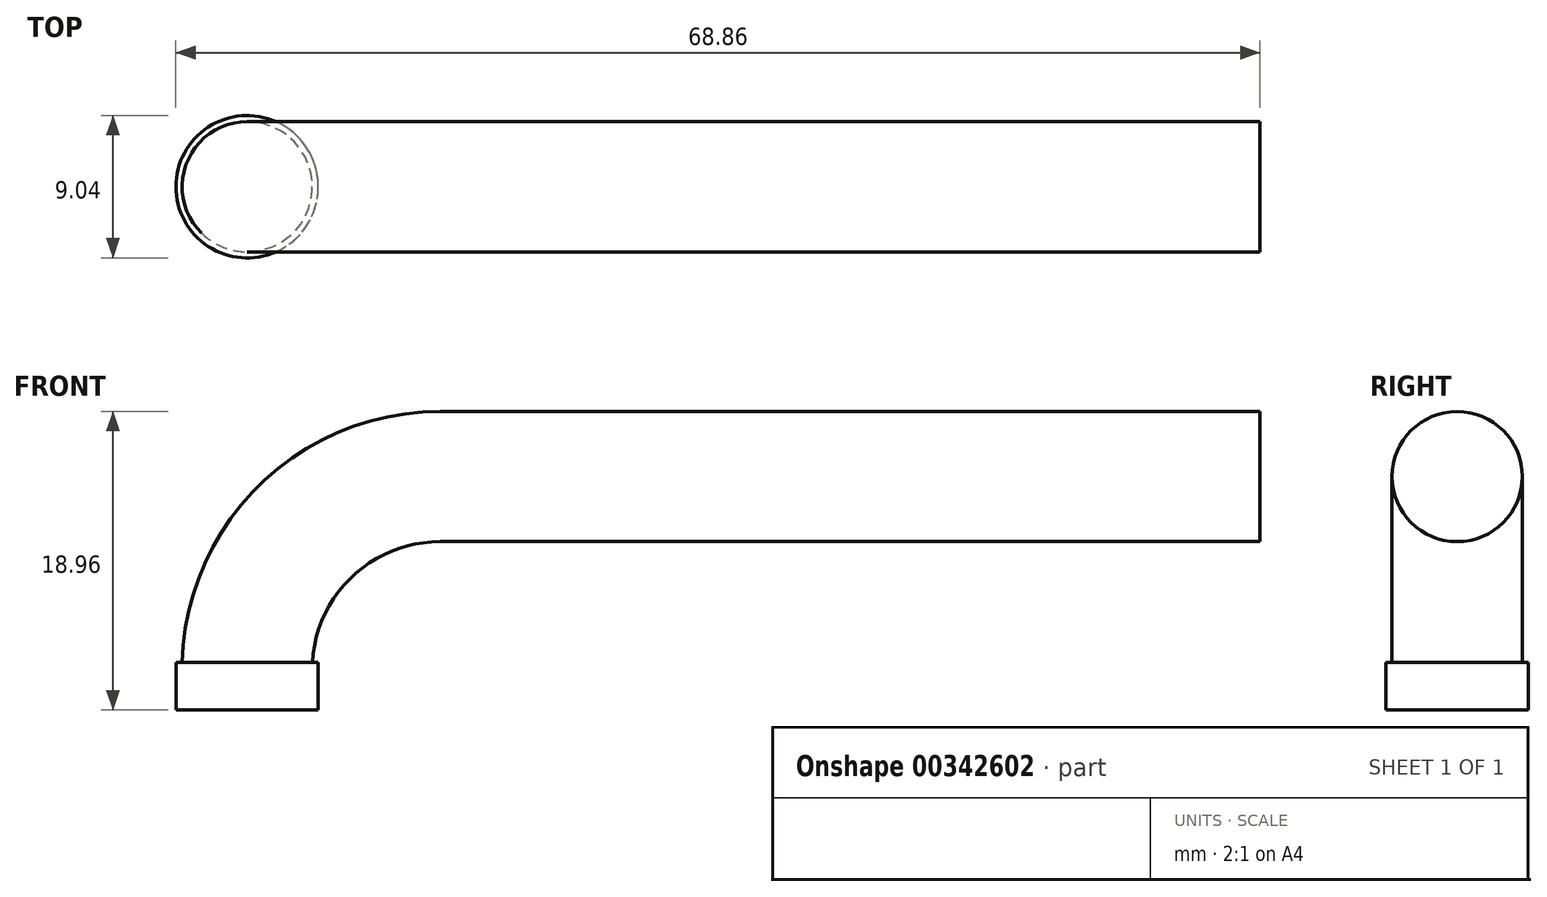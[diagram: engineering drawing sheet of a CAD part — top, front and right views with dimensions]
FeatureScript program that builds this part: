
annotation { "Feature Type Name" : "Feature", "Feature Type Description" : "" }
export const myFeature = defineFeature(function(context is Context, id is Id, definition is map)
    precondition{}
    {
        {
            var Q0;
            Q0=qCreatedBy(makeId("Front.planeOp"),FACE);
            var sketch = newSketch(context, id + "F0", { "sketchPlane" : qUnion([Q0])});
            skLineSegment(sketch, "E0", {"start": v(0, 28.7) * mm, "end": v(-52.1, 28.7) * mm});
            skArc(sketch, "E1", {"start": v(-52.1, 28.7) * mm, "mid": v(-60.75, 25.12) * mm, "end": v(-64.33, 16.46) * mm});
            skLineSegment(sketch, "E2", {"start": v(-52.1, 16.46) * mm, "end": v(-52.1, 28.7) * mm});
            skLineSegment(sketch, "E3", {"start": v(-52.1, 16.46) * mm, "end": v(-64.33, 16.46) * mm});
            skLineSegment(sketch, "E4", {"start": v(-64.33, 16.46) * mm, "end": v(-64.33, 13.88) * mm});
            skSolve(sketch);
        }
        {
            var Q0;
            Q0=qCreatedBy(makeId("Right.planeOp"),FACE);
            var sketch = newSketch(context, id + "F1", { "sketchPlane" : qUnion([Q0])});
            skCircle(sketch, "E5", {"center": v(0, 28.7) * mm, "radius": 4.14 * mm});
            skSolve(sketch);
        }
        {
            var Q0;
            Q0=makeQuery(id+"F1.imprint","IMPRINT",FACE,{"disambiguationData":[TD([[makeQuery(id+"F1.imprint","IMPRINT",EDGE,{"derivedFrom":sQuery(id+"F1.wireOp",EDGE,"E5")}),1.0]])]});
            var Q1;
            Q1=sQuery(id+"F0.wireOp",EDGE,"E0");
            var Q2;
            Q2=sQuery(id+"F0.wireOp",EDGE,"E1");
            var Q3;
            Q3=sQuery(id+"F0.wireOp",EDGE,"E4");
            sweep(context, id + "F2", {"profiles" : qUnion([Q0]), "path" : qUnion([Q1, Q2, Q3])});
        }
        {
            var Q0;
            Q0=makeQuery(id+"F2.opSweep","CAP_FACE",FACE,{"disambiguationData":[OSD([sQuery(id+"F0.wireOp",VERTEX,"E1.end"),sQuery(id+"F1.wireOp",EDGE,"E5")])],"isStart":false});
            var sketch = newSketch(context, id + "F3", { "sketchPlane" : qUnion([Q0])});
            skCircle(sketch, "E6", {"center": v(-64.33, 0) * mm, "radius": 4.52 * mm});
            skSolve(sketch);
        }
        {
            var Q0;
            Q0=makeQuery(id+"F3.imprint","IMPRINT",FACE,{"disambiguationData":[TD([[makeQuery(id+"F3.imprint","IMPRINT",EDGE,{"derivedFrom":makeQuery(id+"F2.opSweep","CAP_EDGE",EDGE,{"disambiguationData":[OSD([sQuery(id+"F0.wireOp",VERTEX,"E1.end"),sQuery(id+"F1.wireOp",EDGE,"E5")])],"isStart":false})}),1.0]])]});
            var Q1;
            Q1=makeQuery(id+"F3.imprint","IMPRINT",FACE,{"disambiguationData":[TD([[makeQuery(id+"F3.imprint","IMPRINT",EDGE,{"derivedFrom":sQuery(id+"F3.wireOp",EDGE,"E6")}),1.0]])]});
            extrude(context, id + "F4", {"entities" : qUnion([Q0, Q1]), "operationType" : NewBodyOperationType.ADD, "oppositeDirection" : true, "depth" : 3 * mm});
        }
    });
